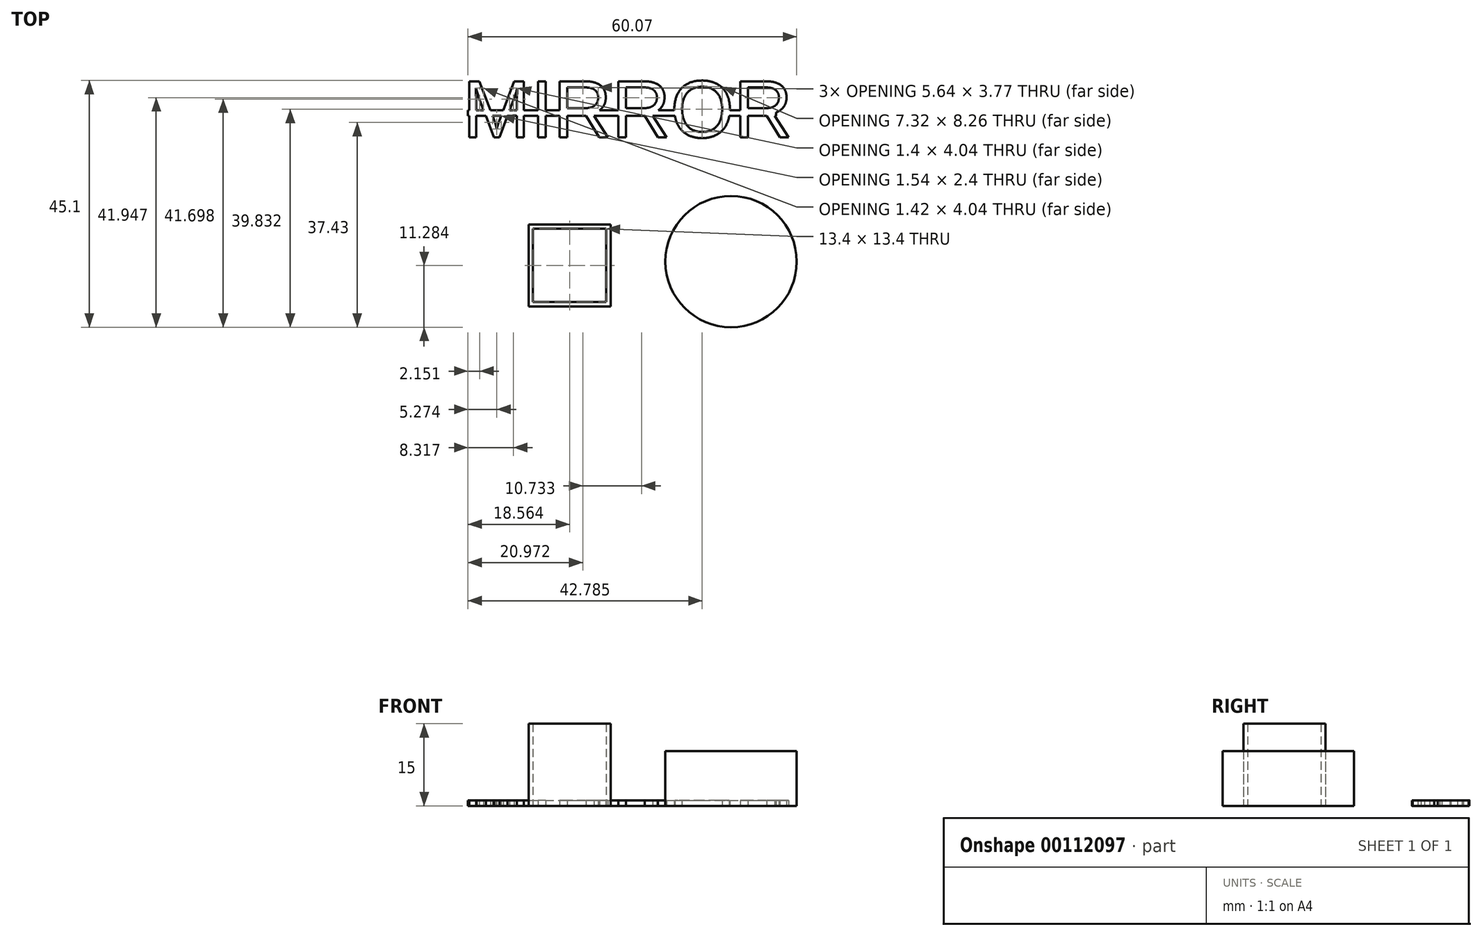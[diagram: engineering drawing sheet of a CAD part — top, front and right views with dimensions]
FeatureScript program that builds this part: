
annotation { "Feature Type Name" : "Feature", "Feature Type Description" : "" }
export const myFeature = defineFeature(function(context is Context, id is Id, definition is map)
    precondition{}
    {
        {
            var Q0;
            Q0=qCreatedBy(makeId("Top.planeOp"),FACE);
            var sketch = newSketch(context, id + "F0", { "sketchPlane" : qUnion([Q0])});
            skLineSegment(sketch, "E0.bottom", {"start": v(-11.14, 6.78) * mm, "end": v(3.86, 6.78) * mm});
            skLineSegment(sketch, "E0.top", {"start": v(-11.14, -8.22) * mm, "end": v(3.86, -8.22) * mm});
            skLineSegment(sketch, "E0.left", {"start": v(-11.14, 6.78) * mm, "end": v(-11.14, -8.22) * mm});
            skLineSegment(sketch, "E0.right", {"start": v(3.86, 6.78) * mm, "end": v(3.86, -8.22) * mm});
            skLineSegment(sketch, "E1.0", {"start": v(-10.34, -7.42) * mm, "end": v(3.06, -7.42) * mm});
            skLineSegment(sketch, "E1.1", {"start": v(-10.34, 5.98) * mm, "end": v(-10.34, -7.42) * mm});
            skLineSegment(sketch, "E1.2", {"start": v(-10.34, 5.98) * mm, "end": v(3.06, 5.98) * mm});
            skLineSegment(sketch, "E1.3", {"start": v(3.06, 5.98) * mm, "end": v(3.06, -7.42) * mm});
            skSolve(sketch);
        }
        {
            var Q0;
            Q0=makeQuery(id+"F0.imprint","IMPRINT",FACE,{"disambiguationData":[TD([[makeQuery(id+"F0.imprint","IMPRINT",EDGE,{"derivedFrom":sQuery(id+"F0.wireOp",EDGE,"E0.bottom")}),-1.0]])]});
            extrude(context, id + "F1", {"entities" : qUnion([Q0]), "depth" : 15 * mm});
        }
        {
            var Q0;
            Q0=qCreatedBy(makeId("Top.planeOp"),FACE);
            var sketch = newSketch(context, id + "F2", { "sketchPlane" : qUnion([Q0])});
            skCircle(sketch, "E2", {"center": v(25.87, 0) * mm, "radius": 12 * mm});
            skSolve(sketch);
        }
        {
            var Q0;
            Q0=makeQuery(id+"F2.imprint","IMPRINT",FACE,{"disambiguationData":[TD([[makeQuery(id+"F2.imprint","IMPRINT",EDGE,{"derivedFrom":sQuery(id+"F2.wireOp",EDGE,"E2")}),1.0]])]});
            extrude(context, id + "F3", {"entities" : qUnion([Q0]), "depth" : 10 * mm, "offsetDistance" : 25 * mm});
        }
        {
            var Q0;
            Q0=qCreatedBy(makeId("Top.planeOp"),FACE);
            var sketch = newSketch(context, id + "F4", { "sketchPlane" : qUnion([Q0])});
            skText(sketch, "E3", { "text": "MIRROR", "fontName": "Arimo-Regular.ttf"});
            skLineSegment(sketch, "E4.bottom", {"start": v(-22.2, 27.68) * mm, "end": v(34.1, 27.68) * mm});
            skLineSegment(sketch, "E4.top", {"start": v(-22.2, 26.63) * mm, "end": v(34.1, 26.63) * mm});
            skLineSegment(sketch, "E4.left", {"start": v(-22.2, 27.68) * mm, "end": v(-22.2, 26.63) * mm});
            skLineSegment(sketch, "E4.right", {"start": v(34.1, 27.68) * mm, "end": v(34.1, 26.63) * mm});
            const initialGuessF4  = {"E3": [-0.02316, 0.02272, 1, 0, 0.0107]};
            skSetInitialGuess(sketch, initialGuessF4);
            skSolve(sketch);
        }
        {
            var Q0;
            Q0 = qSketchRegion(id + "F4", true);
            extrude(context, id + "F5", {"entities" : qUnion([Q0]), "depth" : 1 * mm, "offsetDistance" : 25 * mm});
        }
    });
